# Revit family: Original-allas - veivi - oikeankätinen
name_source: partatom
category: Plumbing Fixtures
revit_build: Autodesk Revit 2015 (Build: 20160512_0715(x64)
units: mm (PartAtom-declared; Revit-internal decimal feet)

## types (2) — shared parameters
Assembly Code = 1336
Depth = 500 mm  [stored 1.64042 ft]
Frame Colour = RAL 9016 - White
Height = 187 mm
Keynote = 523
Manufacturer = Väinö Korpinen Oy
Model = Oval
Support Height = 800 mm  [stored 2.62467 ft]
Thickness = 30 mm  [stored 0.0984252 ft]
URL = https://korpinen.com
Width = 1000 mm  [stored 3.28084 ft]

## per-type parameters (varying)
| type | Colour | Model ID |
| 6202GAM kaide harmaa RAL 7037 | RAL 7037 - Gray | 6202GAM |
| 6202RAM kaide punainen RAL 3003 | RAL 3003 - Red | 6202RAM |

note: [stored X ft] marks values corroborated as IEEE doubles in the binary element streams (Revit-internal decimal feet)

## geometry (parser evidence)
native form markers: Blend x6, Sweep x17
no freeform markers — native parametric forms only
